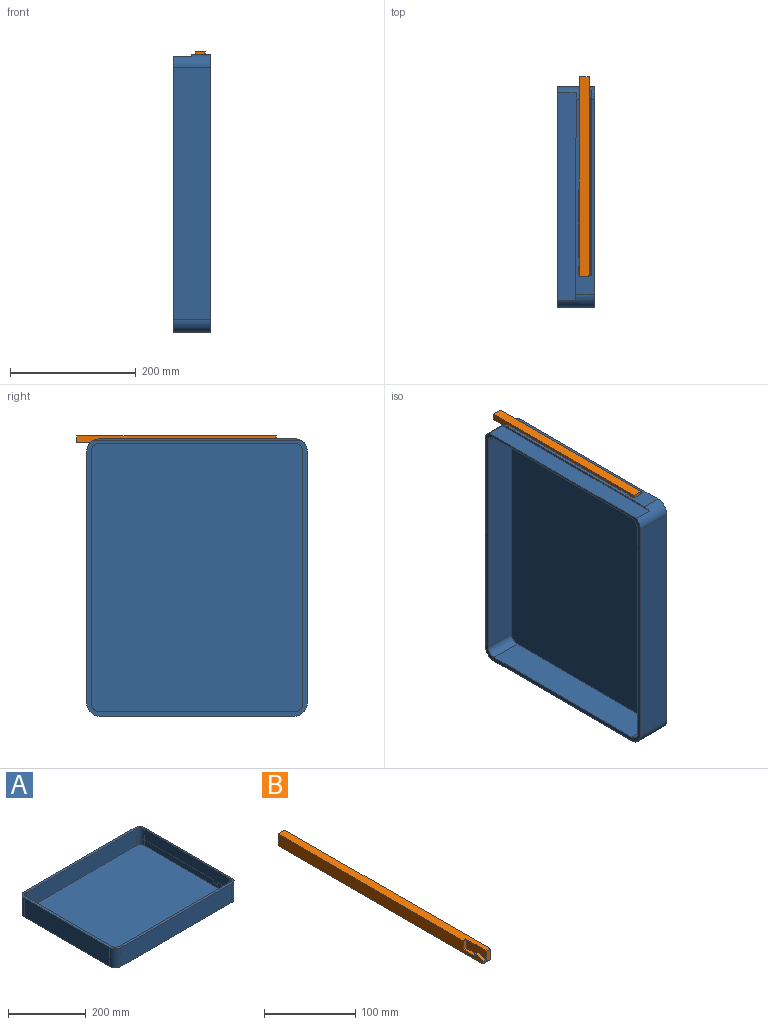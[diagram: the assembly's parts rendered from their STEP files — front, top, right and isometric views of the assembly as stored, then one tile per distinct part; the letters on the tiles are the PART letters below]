
ASSEMBLY  parts=2 mates=1
PART A: 36 faces, bbox 442x351x59.5 mm
  f0: plane 311x30mm, normal (1,0,0), area 3798.8mm2, adj f2,f3,f9,f19,f20,f21,f22,f23
  f1: plane 439x351mm, normal (0,0,1), area 9731.9mm2, adj f2,f3,f4,f5,f6,f7,f8,f10
  f2: cylinder r=20mm len=59.5mm, axis (0,0,-1), area 1541.9mm2, adj f0,f1,f8,f9,f34,f35
  f3: cylinder r=20mm len=59.5mm, axis (0,0,-1), area 1223.7mm2, adj f0,f1,f4,f9,f19,f20,f27,f34
  f4: plane 402x59.5mm, normal (0,1,0), area 23919mm2, adj f1,f3,f5,f9
  f5: cylinder r=20mm len=59.5mm, axis (0,0,-1), area 1869.2mm2, adj f1,f4,f6,f9
  f6: plane 311x59.5mm, normal (-1,0,0), area 18504.5mm2, adj f1,f5,f7,f9
  f7: cylinder r=20mm len=59.5mm, axis (0,0,-1), area 1869.2mm2, adj f1,f6,f8,f9
  f8: plane 402x59.5mm, normal (0,-1,0), area 23919mm2, adj f1,f2,f7,f9
  f9: plane 442x351mm, normal (0,0,-1), area 154798.6mm2, adj f0,f2,f3,f4,f5,f6,f7,f8
  f10: plane 311x52.5mm, normal (-1,0,0), area 16327.5mm2, adj f1,f11,f17,f18
  f11: cylinder r=13mm len=52.5mm, axis (0,0,-1), area 1072.1mm2, adj f1,f10,f12,f18
  f12: plane 402x52.5mm, normal (0,-1,0), area 21105mm2, adj f1,f11,f13,f18
  f13: cylinder r=13mm len=52.5mm, axis (0,0,-1), area 1072.1mm2, adj f1,f12,f14,f18
  f14: plane 311x52.5mm, normal (1,0,0), area 16327.5mm2, adj f1,f13,f15,f18
  f15: cylinder r=13mm len=52.5mm, axis (0,0,-1), area 1072.1mm2, adj f1,f14,f16,f18
  f16: plane 402x52.5mm, normal (0,1,0), area 21105mm2, adj f1,f15,f17,f18
  f17: cylinder r=13mm len=52.5mm, axis (0,0,-1), area 1072.1mm2, adj f1,f10,f16,f18
  f18: plane 428x337mm, normal (0,0,1), area 144090.9mm2, adj f10,f11,f12,f13,f14,f15,f16,f17
  f19: plane 295.95x6mm, normal (0,0,1), area 1749.1mm2, adj f0,f3,f26,f27
  f20: plane 266.07x6mm, normal (0,0,-1), area 1569.8mm2, adj f0,f3,f21,f27
  f21: plane 8.04x6mm, normal (0,1,0), area 48.2mm2, adj f0,f20,f22,f27
  f22: plane 10.99x6mm, normal (0,0.26,-0.97), area 68.3mm2, adj f0,f21,f23,f27
  f23: plane 6x4.01mm, normal (0,0,-1), area 24.1mm2, adj f0,f22,f24,f27
  f24: plane 11x6mm, normal (0,-1,0), area 66mm2, adj f0,f23,f25,f27
  f25: plane 14.88x6mm, normal (0,0,-1), area 89.3mm2, adj f0,f24,f26,f27
  f26: plane 20x6mm, normal (0,1,0), area 120mm2, adj f0,f19,f25,f27
  f27: plane 295.95x20mm, normal (1,0,0), area 5770.3mm2, adj f3,f19,f20,f21,f22,f23,f24,f25
  f28: plane 6x3.45mm, normal (0,-1,0), area 20.7mm2, adj f0,f29,f32,f33
  f29: plane 9.8x6mm, normal (0,0,-1), area 58.8mm2, adj f0,f28,f30,f33
  f30: plane 6x5.8mm, normal (0,1,0), area 34.8mm2, adj f0,f29,f31,f33
  f31: plane 6x1.06mm, normal (0,0,1), area 6.4mm2, adj f0,f30,f32,f33
  f32: plane 8.74x6mm, normal (0,-0.26,0.97), area 54.3mm2, adj f0,f28,f31,f33
  f33: plane 9.8x5.8mm, normal (1,0,0), area 46.6mm2, adj f28,f29,f30,f31,f32
  f34: plane 332.07x3mm, normal (0,0,1), area 975.8mm2, adj f0,f2,f3,f35
  f35: plane 332.07x29.5mm, normal (1,0,0), area 9796.1mm2, adj f1,f2,f3,f34
PART B: 17 faces, bbox 10.5x317.8x15.9 mm
  f0: plane 316.83x10.5mm, normal (0,0,1), area 3188.2mm2, adj f1,f12,f13,f14,f15,f16
  f1: cylinder r=1mm len=4.5mm, axis (1,0,0), area 7.1mm2, adj f0,f2,f13,f16
  f2: plane 9.9x4.5mm, normal (0,-1,0), area 44.5mm2, adj f1,f3,f13,f16
  f3: cylinder r=1mm len=4.5mm, axis (1,0,0), area 7.1mm2, adj f2,f4,f13,f16
  f4: plane 15.82x4.5mm, normal (0,0,1), area 71.2mm2, adj f3,f5,f13,f16
  f5: plane 4.5x2.46mm, normal (0,1,0), area 11.1mm2, adj f4,f6,f13,f16
  f6: cylinder r=1mm len=4.5mm, axis (1,0,0), area 8.3mm2, adj f5,f7,f13,f16
  f7: plane 11.95x4.5mm, normal (0,-0.26,0.97), area 55.7mm2, adj f6,f8,f13,f16
  f8: cylinder r=1mm len=4.5mm, axis (1,0,0), area 5.9mm2, adj f7,f9,f13,f16
  f9: plane 13.87x10.5mm, normal (0,-1,0), area 93.2mm2, adj f8,f10,f13,f14,f15,f16
  f10: cylinder r=1mm len=10.5mm, axis (1,0,0), area 16.5mm2, adj f9,f11,f13,f15
  f11: plane 316.83x10.5mm, normal (0,0,-1), area 3326.7mm2, adj f10,f12,f13,f15
  f12: plane 15.87x10.5mm, normal (0,1,0), area 166.6mm2, adj f0,f11,f13,f15
  f13: plane 317.83x15.87mm, normal (-1,0,0), area 4703.3mm2, adj f0,f1,f2,f3,f4,f5,f6,f7
  f14: cylinder r=1mm len=6mm, axis (-1,0,0), area 9.4mm2, adj f0,f9,f15,f16
  f15: plane 317.83x15.87mm, normal (1,0,0), area 5043.4mm2, adj f0,f9,f10,f11,f12,f14
  f16: plane 31.77x12.66mm, normal (-1,0,0), area 340.1mm2, adj f0,f1,f2,f3,f4,f5,f6,f7
PLACE A rot(axis=(0,-1,0),90deg) t=(16.61,-32.74,-225.5)mm
PLACE B rot(axis=(0,-1,0),90deg) t=(17.07,-32.76,-227)mm
MATE planar B.f13 <-> A.f27  axis (0,0,-1) through (-7.93,15.87,-10.5)mm
